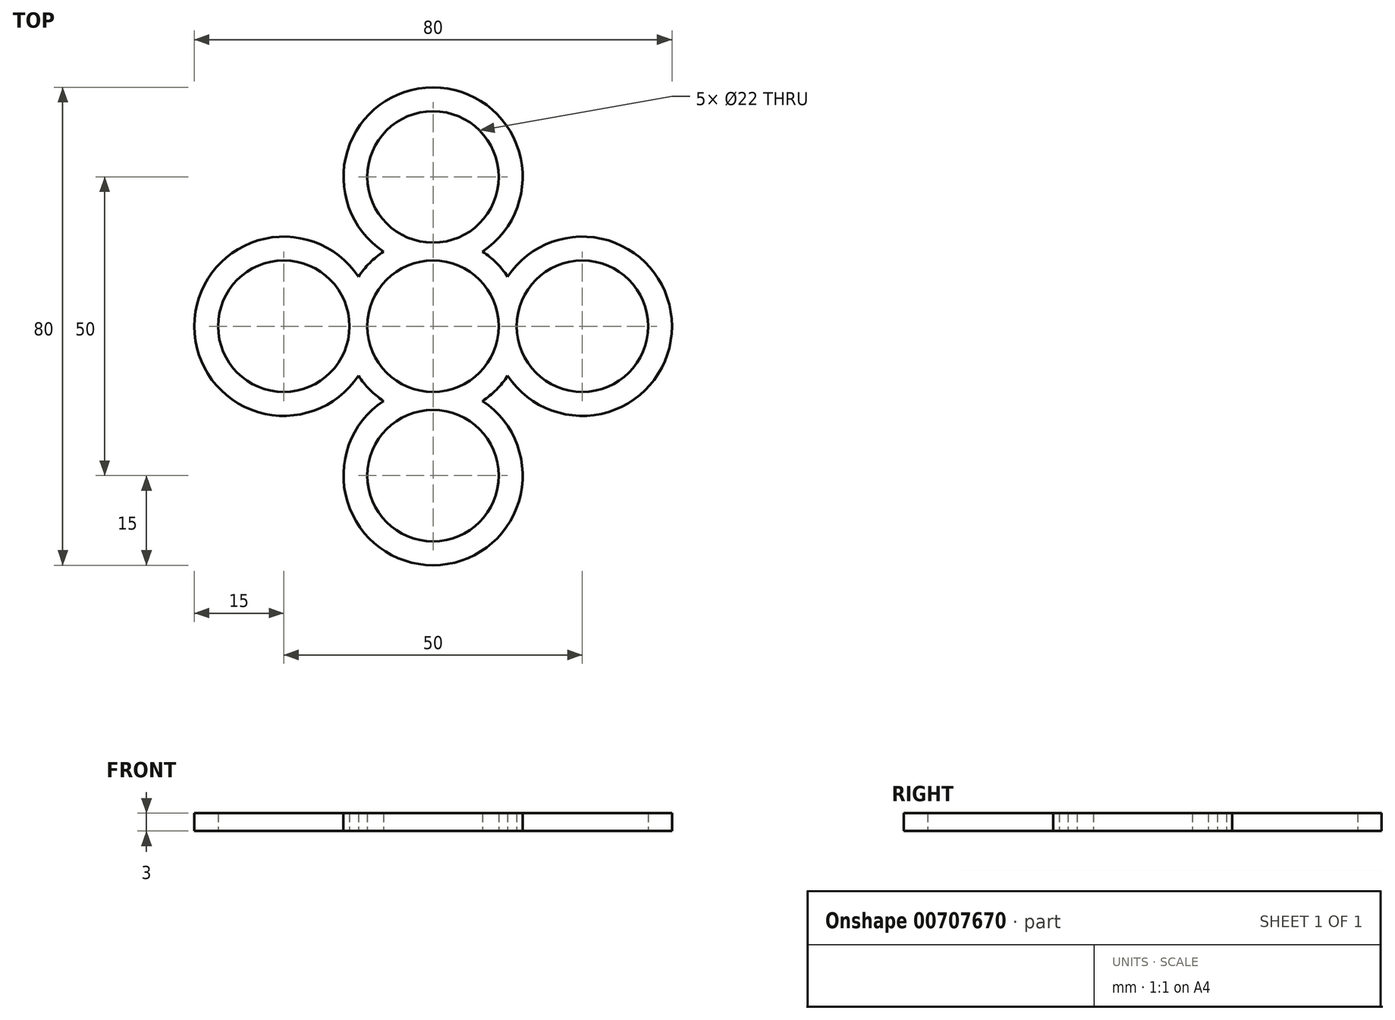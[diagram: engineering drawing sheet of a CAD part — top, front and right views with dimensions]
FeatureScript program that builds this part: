
annotation { "Feature Type Name" : "Feature", "Feature Type Description" : "" }
export const myFeature = defineFeature(function(context is Context, id is Id, definition is map)
    precondition{}
    {
        {
            var Q0;
            Q0=qCreatedBy(makeId("Top.planeOp"),FACE);
            var sketch = newSketch(context, id + "F0", { "sketchPlane" : qUnion([Q0])});
            skCircle(sketch, "E0", {"center": v(0, 0) * mm, "radius": 11 * mm});
            skLineSegment(sketch, "E1", {"start": v(0, 0) * mm, "end": v(-25, 0) * mm});
            skCircle(sketch, "E2", {"center": v(-25, 0) * mm, "radius": 11 * mm});
            skArc(sketch, "E3", {"start": v(-12.5, 8.3) * mm, "mid": v(-40, 0) * mm, "end": v(-12.5, -8.3) * mm});
            skLineSegment(sketch, "E4", {"start": v(0, 0) * mm, "end": v(0, 25) * mm});
            skLineSegment(sketch, "E5", {"start": v(0, 0) * mm, "end": v(0, -25) * mm});
            skLineSegment(sketch, "E6", {"start": v(0, 0) * mm, "end": v(25, 0) * mm});
            skCircle(sketch, "E7", {"center": v(25, 0) * mm, "radius": 11 * mm});
            skCircle(sketch, "E8", {"center": v(0, 25) * mm, "radius": 11 * mm});
            skCircle(sketch, "E9", {"center": v(0, -25) * mm, "radius": 11 * mm});
            skArc(sketch, "E10", {"start": v(8.3, 12.5) * mm, "mid": v(0, 40) * mm, "end": v(-8.3, 12.5) * mm});
            skArc(sketch, "E11", {"start": v(12.5, -8.3) * mm, "mid": v(40, 0) * mm, "end": v(12.5, 8.3) * mm});
            skArc(sketch, "E12", {"start": v(-8.3, -12.5) * mm, "mid": v(0, -40) * mm, "end": v(8.3, -12.5) * mm});
            skArc(sketch, "E13.trimOffspring", {"start": v(-12.5, -8.3) * mm, "mid": v(-10.6, -10.6) * mm, "end": v(-8.3, -12.5) * mm});
            skArc(sketch, "E14.trimOffspring", {"start": v(-8.3, 12.5) * mm, "mid": v(-10.6, 10.6) * mm, "end": v(-12.5, 8.3) * mm});
            skArc(sketch, "E15.trimOffspring", {"start": v(12.5, 8.3) * mm, "mid": v(10.6, 10.6) * mm, "end": v(8.3, 12.5) * mm});
            skArc(sketch, "E16.trimOffspring", {"start": v(8.3, -12.5) * mm, "mid": v(10.6, -10.6) * mm, "end": v(12.5, -8.3) * mm});
            skSolve(sketch);
        }
        {
            var Q0;
            Q0 = qSketchRegion(id + "F0", true);
            extrude(context, id + "F1", {"entities" : qUnion([Q0]), "depth" : 3 * mm, "offsetDistance" : 25 * mm});
        }
    });
